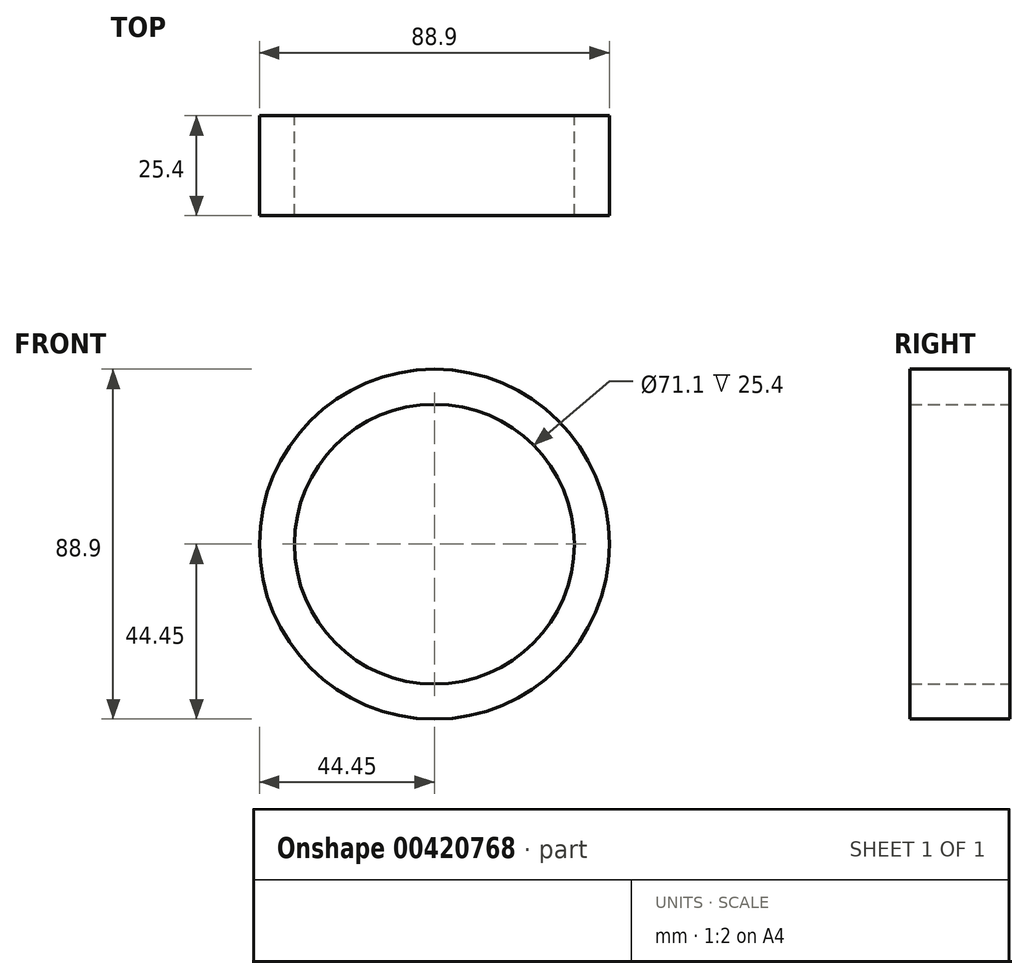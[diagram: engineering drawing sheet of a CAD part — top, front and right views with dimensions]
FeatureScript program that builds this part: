
annotation { "Feature Type Name" : "Feature", "Feature Type Description" : "" }
export const myFeature = defineFeature(function(context is Context, id is Id, definition is map)
    precondition{}
    {
        {
            var Q0;
            Q0=qCreatedBy(makeId("Front.planeOp"),FACE);
            var sketch = newSketch(context, id + "F0", { "sketchPlane" : qUnion([Q0])});
            skCircle(sketch, "E0", {"center": v(0, 0) * mm, "radius": 44.45 * mm});
            skLineSegment(sketch, "E1", {"start": v(-44.45, 0) * mm, "end": v(-35.55, 0) * mm});
            skCircle(sketch, "E2", {"center": v(0, 0) * mm, "radius": 35.55 * mm});
            skSolve(sketch);
        }
        {
            var Q0;
            Q0=makeQuery(id+"F0.imprint","IMPRINT",FACE,{"disambiguationData":[TD([[makeQuery(id+"F0.imprint","IMPRINT",EDGE,{"derivedFrom":sQuery(id+"F0.wireOp",EDGE,"E0")}),1.0]])]});
            extrude(context, id + "F1", {"entities" : qUnion([Q0]), "depth" : 25.4 * mm});
        }
    });
